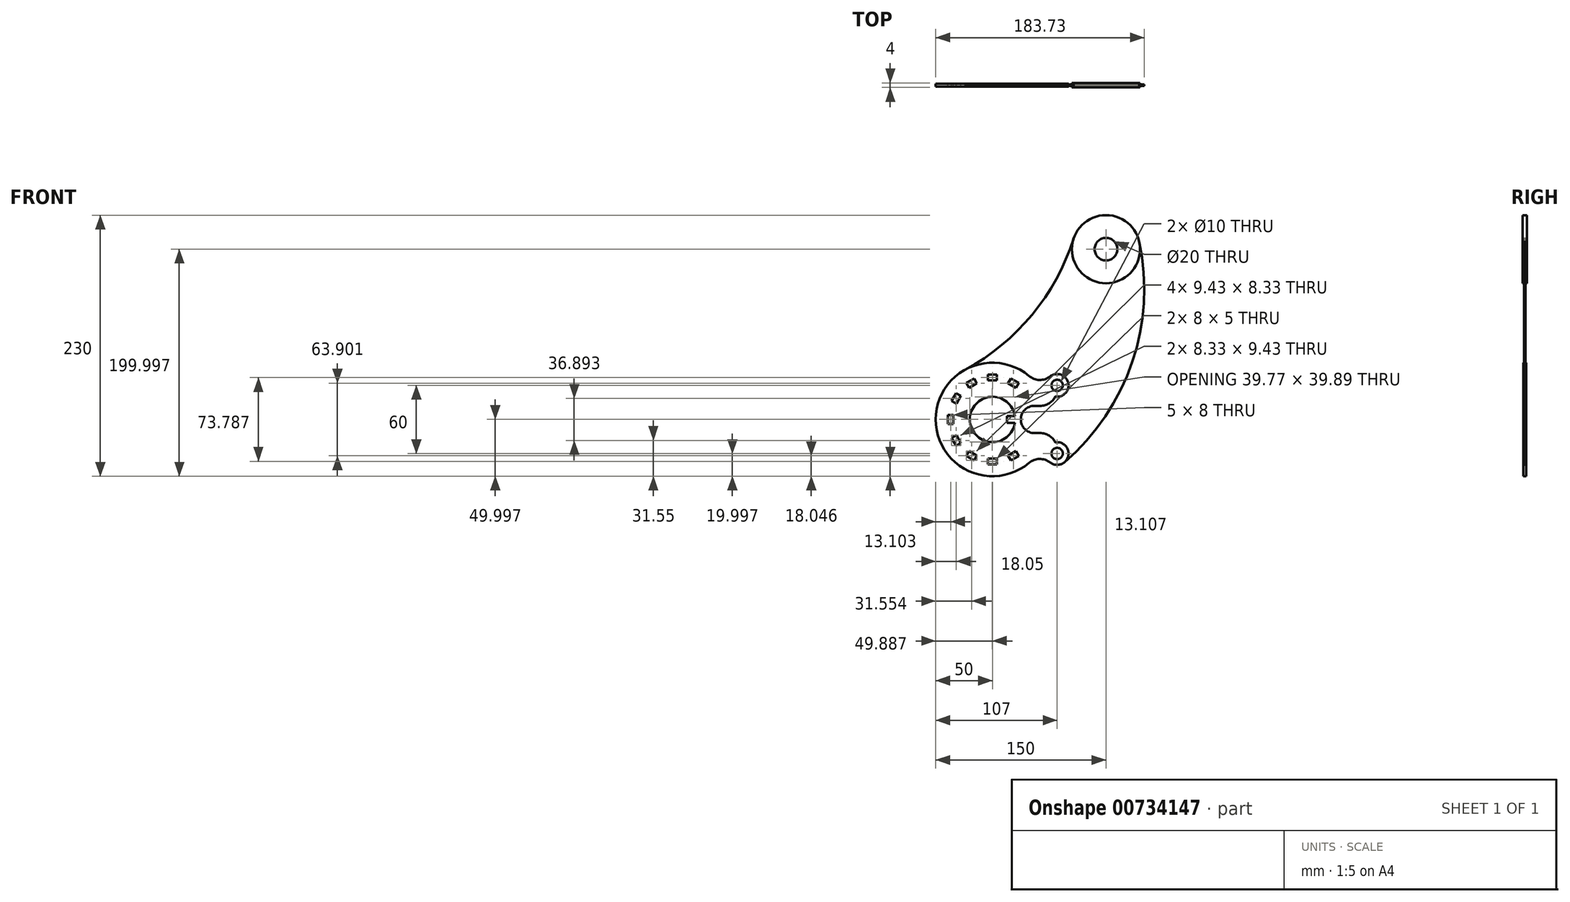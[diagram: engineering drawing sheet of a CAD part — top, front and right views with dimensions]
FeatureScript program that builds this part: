
annotation { "Feature Type Name" : "Feature", "Feature Type Description" : "" }
export const myFeature = defineFeature(function(context is Context, id is Id, definition is map)
    precondition{}
    {
        {
            var Q0;
            Q0=qCreatedBy(makeId("Front.planeOp"),FACE);
            var sketch = newSketch(context, id + "F0", { "sketchPlane" : qUnion([Q0])});
            skArc(sketch, "E0", {"start": v(-12.35, -31.4) * mm, "mid": v(-52.12, -34.4) * mm, "end": v(-12.35, -37.4) * mm});
            skLineSegment(sketch, "E1", {"start": v(-12.35, -31.4) * mm, "end": v(-19.35, -31.4) * mm});
            skLineSegment(sketch, "E2", {"start": v(-19.35, -31.4) * mm, "end": v(-19.35, -37.4) * mm});
            skLineSegment(sketch, "E3", {"start": v(-19.35, -37.4) * mm, "end": v(-12.35, -37.4) * mm});
            skArc(sketch, "E4", {"start": v(0, 3.93) * mm, "mid": v(-82.12, -34.4) * mm, "end": v(0, -72.71) * mm});
            skLineSegment(sketch, "E5.bottom", {"start": v(-28.12, 0) * mm, "end": v(-36.12, 0) * mm});
            skLineSegment(sketch, "E5.top", {"start": v(-28.12, 5) * mm, "end": v(-36.12, 5) * mm});
            skLineSegment(sketch, "E5.left", {"start": v(-28.12, 0) * mm, "end": v(-28.12, 5) * mm});
            skLineSegment(sketch, "E5.right", {"start": v(-36.12, 0) * mm, "end": v(-36.12, 5) * mm});
            skPoint(sketch, "E5.middle", {"position": v(-32.12, 2.5) * mm});
            skLineSegment(sketch, "E6.1.0", {"start": v(-48.35, 1.72) * mm, "end": v(-55.28, -2.28) * mm});
            skLineSegment(sketch, "E6.1.1", {"start": v(-45.85, -2.6) * mm, "end": v(-52.78, -6.6) * mm});
            skPoint(sketch, "E6.1.2", {"position": v(-50.57, -2.44) * mm});
            skLineSegment(sketch, "E6.1.3", {"start": v(-45.85, -2.6) * mm, "end": v(-48.35, 1.72) * mm});
            skLineSegment(sketch, "E6.1.4", {"start": v(-52.78, -6.6) * mm, "end": v(-55.28, -2.28) * mm});
            skLineSegment(sketch, "E6.2.0", {"start": v(-64.24, -11.23) * mm, "end": v(-68.24, -18.16) * mm});
            skLineSegment(sketch, "E6.2.1", {"start": v(-59.9, -13.73) * mm, "end": v(-63.9, -20.66) * mm});
            skPoint(sketch, "E6.2.2", {"position": v(-64.07, -15.95) * mm});
            skLineSegment(sketch, "E6.2.3", {"start": v(-59.9, -13.73) * mm, "end": v(-64.24, -11.23) * mm});
            skLineSegment(sketch, "E6.2.4", {"start": v(-63.9, -20.66) * mm, "end": v(-68.24, -18.16) * mm});
            skLineSegment(sketch, "E6.3.0", {"start": v(-71.51, -30.4) * mm, "end": v(-71.51, -38.4) * mm});
            skLineSegment(sketch, "E6.3.1", {"start": v(-66.51, -30.4) * mm, "end": v(-66.51, -38.4) * mm});
            skPoint(sketch, "E6.3.2", {"position": v(-69.01, -34.4) * mm});
            skLineSegment(sketch, "E6.3.3", {"start": v(-66.51, -30.4) * mm, "end": v(-71.51, -30.4) * mm});
            skLineSegment(sketch, "E6.3.4", {"start": v(-66.51, -38.4) * mm, "end": v(-71.51, -38.4) * mm});
            skLineSegment(sketch, "E6.4.0", {"start": v(-68.24, -50.63) * mm, "end": v(-64.24, -57.55) * mm});
            skLineSegment(sketch, "E6.4.1", {"start": v(-63.9, -48.13) * mm, "end": v(-59.9, -55.05) * mm});
            skPoint(sketch, "E6.4.2", {"position": v(-64.07, -52.84) * mm});
            skLineSegment(sketch, "E6.4.3", {"start": v(-63.9, -48.13) * mm, "end": v(-68.24, -50.63) * mm});
            skLineSegment(sketch, "E6.4.4", {"start": v(-59.9, -55.05) * mm, "end": v(-64.24, -57.55) * mm});
            skLineSegment(sketch, "E6.5.0", {"start": v(-55.28, -66.5) * mm, "end": v(-48.35, -70.5) * mm});
            skLineSegment(sketch, "E6.5.1", {"start": v(-52.78, -62.18) * mm, "end": v(-45.85, -66.18) * mm});
            skPoint(sketch, "E6.5.2", {"position": v(-50.57, -66.34) * mm});
            skLineSegment(sketch, "E6.5.3", {"start": v(-52.78, -62.18) * mm, "end": v(-55.28, -66.5) * mm});
            skLineSegment(sketch, "E6.5.4", {"start": v(-45.85, -66.18) * mm, "end": v(-48.35, -70.5) * mm});
            skLineSegment(sketch, "E6.6.0", {"start": v(-36.12, -73.79) * mm, "end": v(-28.12, -73.79) * mm});
            skLineSegment(sketch, "E6.6.1", {"start": v(-36.12, -68.79) * mm, "end": v(-28.12, -68.79) * mm});
            skPoint(sketch, "E6.6.2", {"position": v(-32.12, -71.29) * mm});
            skLineSegment(sketch, "E6.6.3", {"start": v(-36.12, -68.79) * mm, "end": v(-36.12, -73.79) * mm});
            skLineSegment(sketch, "E6.6.4", {"start": v(-28.12, -68.79) * mm, "end": v(-28.12, -73.79) * mm});
            skLineSegment(sketch, "E6.7.0", {"start": v(-15.89, -70.5) * mm, "end": v(-8.96, -66.5) * mm});
            skLineSegment(sketch, "E6.7.1", {"start": v(-18.39, -66.18) * mm, "end": v(-11.46, -62.18) * mm});
            skPoint(sketch, "E6.7.2", {"position": v(-13.67, -66.34) * mm});
            skLineSegment(sketch, "E6.7.3", {"start": v(-18.39, -66.18) * mm, "end": v(-15.89, -70.5) * mm});
            skLineSegment(sketch, "E6.7.4", {"start": v(-11.46, -62.18) * mm, "end": v(-8.96, -66.5) * mm});
            skLineSegment(sketch, "E6.11.0", {"start": v(-8.96, -2.28) * mm, "end": v(-15.89, 1.72) * mm});
            skLineSegment(sketch, "E6.11.1", {"start": v(-11.46, -6.6) * mm, "end": v(-18.39, -2.6) * mm});
            skPoint(sketch, "E6.11.2", {"position": v(-13.67, -2.44) * mm});
            skLineSegment(sketch, "E6.11.3", {"start": v(-11.46, -6.6) * mm, "end": v(-8.96, -2.28) * mm});
            skLineSegment(sketch, "E6.11.4", {"start": v(-18.39, -2.6) * mm, "end": v(-15.89, 1.72) * mm});
            skCircle(sketch, "E7", {"center": v(67.88, 115.6) * mm, "radius": 30 * mm});
            skCircle(sketch, "E8", {"center": v(67.88, 115.6) * mm, "radius": 10 * mm});
            skLineSegment(sketch, "E9", {"start": v(-38.61, 115.6) * mm, "end": v(139.63, 115.6) * mm, "construction": true});
            skLineSegment(sketch, "E10", {"start": v(-148.84, -34.4) * mm, "end": v(105.47, -34.4) * mm, "construction": true});
            skLineSegment(sketch, "E11", {"start": v(-32.12, 109.99) * mm, "end": v(-32.12, -119.75) * mm, "construction": true});
            skLineSegment(sketch, "E12", {"start": v(67.88, 181.63) * mm, "end": v(67.88, 72.1) * mm, "construction": true});
            skArc(sketch, "E13", {"start": v(4.88, -22.4) * mm, "mid": v(-7.12, -34.4) * mm, "end": v(4.88, -46.4) * mm});
            skCircle(sketch, "E14", {"center": v(24.88, -4.4) * mm, "radius": 5 * mm});
            skCircle(sketch, "E15", {"center": v(24.88, -64.4) * mm, "radius": 5 * mm});
            skArc(sketch, "E16", {"start": v(23.22, -14.25) * mm, "mid": v(34.58, -1.97) * mm, "end": v(18.78, 3.53) * mm});
            skArc(sketch, "E17", {"start": v(18.78, -72.32) * mm, "mid": v(34.58, -66.81) * mm, "end": v(23.22, -54.53) * mm});
            skArc(sketch, "E18", {"start": v(-55.95, 9.56) * mm, "mid": v(2.83, 57.9) * mm, "end": v(39.3, 124.7) * mm});
            skArc(sketch, "E19", {"start": v(31.37, -72) * mm, "mid": v(90.98, 15.86) * mm, "end": v(97.22, 121.86) * mm});
            skLineSegment(sketch, "E20", {"start": v(4.88, 24.24) * mm, "end": v(4.88, -81.64) * mm, "construction": true});
            skArc(sketch, "E21", {"start": v(18.78, -72.32) * mm, "mid": v(9.32, -69.21) * mm, "end": v(0, -72.71) * mm});
            skArc(sketch, "E22", {"start": v(0, 3.93) * mm, "mid": v(9.32, 0.42) * mm, "end": v(18.78, 3.53) * mm});
            skLineSegment(sketch, "E23", {"start": v(4.88, -22.4) * mm, "end": v(9.88, -22.4) * mm});
            skArc(sketch, "E24", {"start": v(9.88, -22.4) * mm, "mid": v(17.7, -20.2) * mm, "end": v(23.22, -14.25) * mm});
            skLineSegment(sketch, "E25.MirrorCS", {"start": v(4.88, -46.4) * mm, "end": v(9.88, -46.4) * mm});
            skArc(sketch, "E26", {"start": v(23.22, -54.53) * mm, "mid": v(17.7, -48.59) * mm, "end": v(9.88, -46.4) * mm});
            skSolve(sketch);
        }
        {
            var Q0;
            Q0=makeQuery(id+"F0.imprint","IMPRINT",FACE,{"disambiguationData":[TD([[makeQuery(id+"F0.imprint","IMPRINT",EDGE,{"derivedFrom":sQuery(id+"F0.wireOp",EDGE,"E0")}),-1.0]])]});
            extrude(context, id + "F1", {"entities" : qUnion([Q0]), "endBound" : BoundingType.SYMMETRIC, "depth" : 2.3 * mm, "offsetDistance" : 25 * mm});
        }
        {
            var Q0;
            Q0=makeQuery(id+"F0.imprint","IMPRINT",FACE,{"disambiguationData":[TD([[makeQuery(id+"F0.imprint","IMPRINT",EDGE,{"derivedFrom":sQuery(id+"F0.wireOp",EDGE,"E8")}),-1.0]])]});
            extrude(context, id + "F2", {"entities" : qUnion([Q0]), "endBound" : BoundingType.SYMMETRIC, "depth" : 4 * mm, "offsetDistance" : 25 * mm});
        }
        {
            var Q0;
            Q0=makeQuery(id+"F0.imprint","IMPRINT",FACE,{"disambiguationData":[TD([[makeQuery(id+"F0.imprint","IMPRINT",EDGE,{"derivedFrom":sQuery(id+"F0.wireOp",EDGE,"E13")}),1.0]])]});
            extrude(context, id + "F3", {"entities" : qUnion([Q0]), "endBound" : BoundingType.SYMMETRIC, "depth" : 1.2 * mm, "offsetDistance" : 25 * mm});
        }
    });
